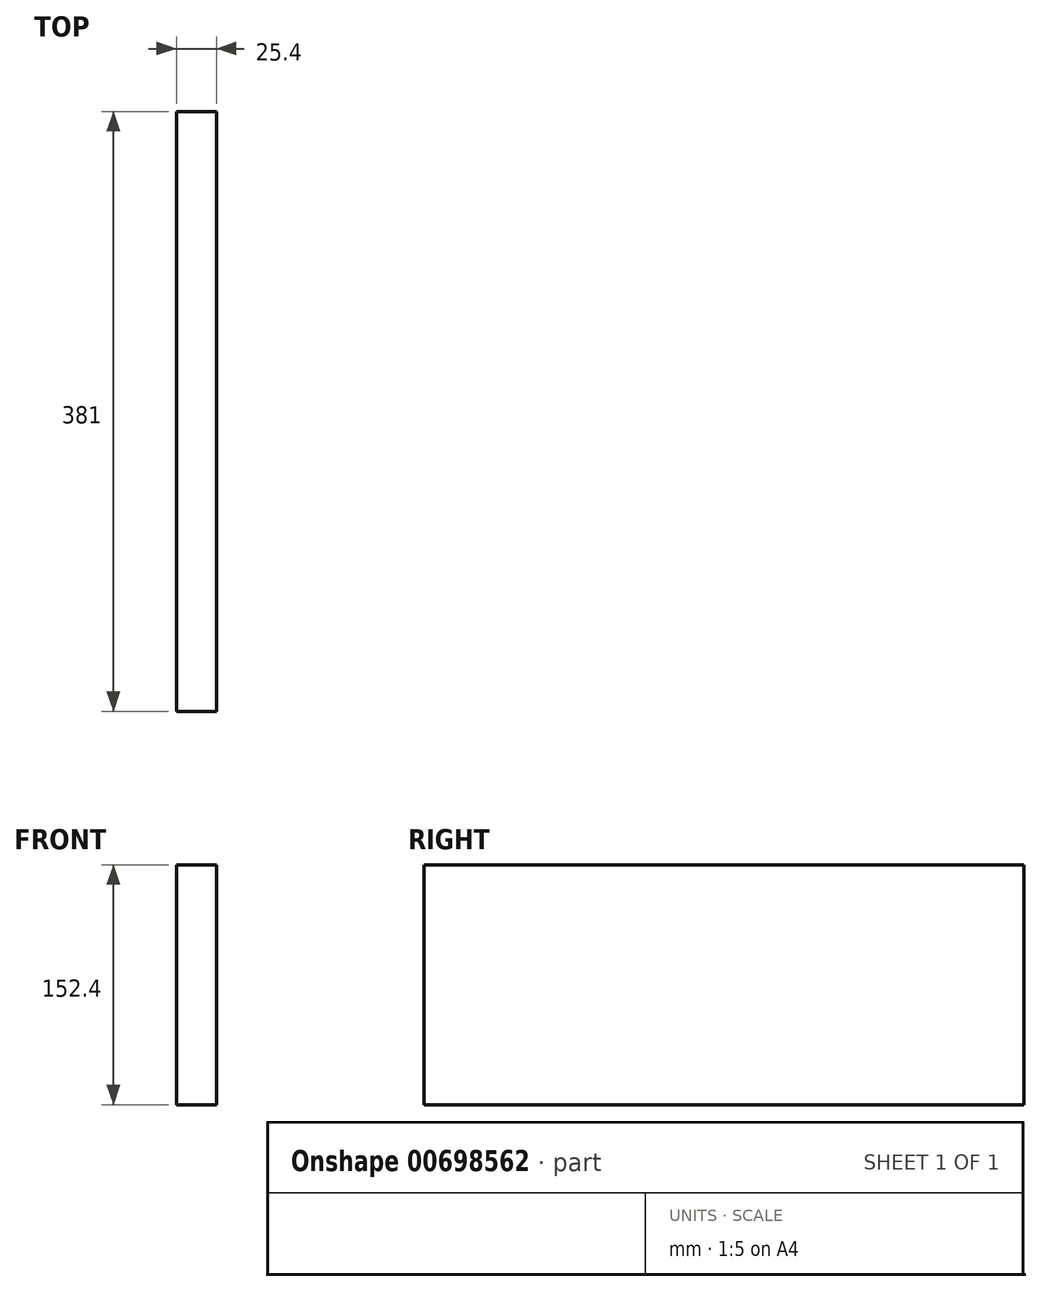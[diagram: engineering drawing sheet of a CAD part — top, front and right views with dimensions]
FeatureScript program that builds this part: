
annotation { "Feature Type Name" : "Feature", "Feature Type Description" : "" }
export const myFeature = defineFeature(function(context is Context, id is Id, definition is map)
    precondition{}
    {
        {
            var Q0;
            Q0=qCreatedBy(makeId("Front.planeOp"),FACE);
            var sketch = newSketch(context, id + "F0", { "sketchPlane" : qUnion([Q0])});
            skLineSegment(sketch, "E0.bottom", {"start": v(-273.22, 69.54) * mm, "end": v(107.78, 69.54) * mm});
            skLineSegment(sketch, "E0.top", {"start": v(-273.22, -82.86) * mm, "end": v(107.78, -82.86) * mm});
            skLineSegment(sketch, "E0.left", {"start": v(-273.22, 69.54) * mm, "end": v(-273.22, -82.86) * mm});
            skLineSegment(sketch, "E0.right", {"start": v(107.78, 69.54) * mm, "end": v(107.78, -82.86) * mm});
            skSolve(sketch);
        }
        {
            var Q0;
            Q0=makeQuery(id+"F0.imprint","IMPRINT",FACE,{"disambiguationData":[TD([[makeQuery(id+"F0.imprint","IMPRINT",EDGE,{"derivedFrom":sQuery(id+"F0.wireOp",EDGE,"E0.bottom")}),-1.0]])]});
            extrude(context, id + "F1", {"entities" : qUnion([Q0]), "depth" : 25.4 * mm, "offsetDistance" : 25.4 * mm});
        }
        {
            var Q0;
            Q0=makeQuery(id+"F1.opExtrude","SWEPT_BODY",BODY,{"disambiguationData":[OSD([sQuery(id+"F0.wireOp",EDGE,"E0.bottom"),sQuery(id+"F0.wireOp",EDGE,"E0.top"),sQuery(id+"F0.wireOp",EDGE,"E0.left"),sQuery(id+"F0.wireOp",EDGE,"E0.right")])]});
            deleteBodies(context, id + "F2", {"entities" : qUnion([Q0])});
        }
        {
            var Q0;
            Q0=qCreatedBy(makeId("Right.planeOp"),FACE);
            var sketch = newSketch(context, id + "F3", { "sketchPlane" : qUnion([Q0])});
            skLineSegment(sketch, "E1.bottom", {"start": v(0, 0) * mm, "end": v(-381, 0) * mm});
            skLineSegment(sketch, "E1.top", {"start": v(0, 152.4) * mm, "end": v(-381, 152.4) * mm});
            skLineSegment(sketch, "E1.left", {"start": v(0, 0) * mm, "end": v(0, 152.4) * mm});
            skLineSegment(sketch, "E1.right", {"start": v(-381, 0) * mm, "end": v(-381, 152.4) * mm});
            skSolve(sketch);
        }
        {
            var Q0;
            Q0=makeQuery(id+"F3.imprint","IMPRINT",FACE,{"disambiguationData":[TD([[makeQuery(id+"F3.imprint","IMPRINT",EDGE,{"derivedFrom":sQuery(id+"F3.wireOp",EDGE,"E1.bottom")}),-1.0]])]});
            extrude(context, id + "F4", {"entities" : qUnion([Q0]), "depth" : 25.4 * mm, "offsetDistance" : 25.4 * mm});
        }
    });
